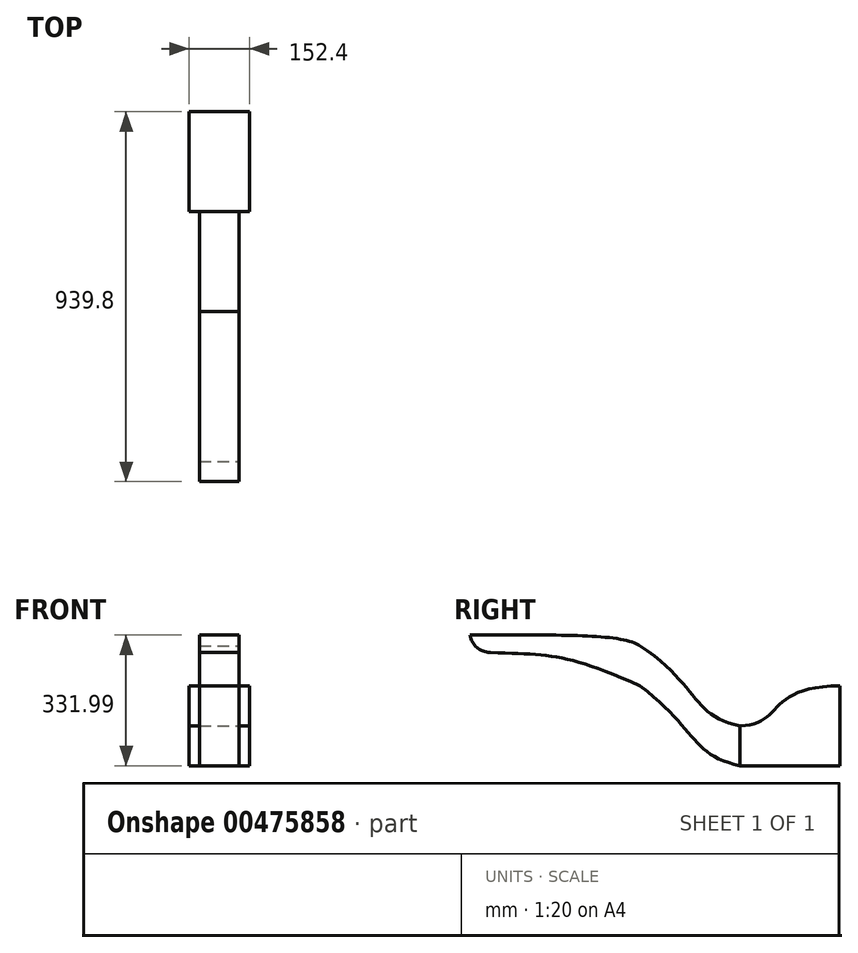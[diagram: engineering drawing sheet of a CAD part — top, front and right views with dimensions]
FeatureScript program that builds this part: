
annotation { "Feature Type Name" : "Feature", "Feature Type Description" : "" }
export const myFeature = defineFeature(function(context is Context, id is Id, definition is map)
    precondition{}
    {
        {
            var Q0;
            Q0=qCreatedBy(makeId("Top.planeOp"),FACE);
            var sketch = newSketch(context, id + "F0", { "sketchPlane" : qUnion([Q0])});
            skLineSegment(sketch, "E0.bottom", {"start": v(63.5, -381) * mm, "end": v(-63.5, -381) * mm});
            skLineSegment(sketch, "E0.top", {"start": v(63.5, 381) * mm, "end": v(-63.5, 381) * mm});
            skLineSegment(sketch, "E0.left", {"start": v(63.5, -381) * mm, "end": v(63.5, 381) * mm});
            skLineSegment(sketch, "E0.right", {"start": v(-63.5, -381) * mm, "end": v(-63.5, 381) * mm});
            skPoint(sketch, "E0.middle", {"position": v(0, 0) * mm});
            skSolve(sketch);
        }
        {
            var Q0;
            Q0=makeQuery(id+"F0.imprint","IMPRINT",FACE,{"disambiguationData":[TD([[makeQuery(id+"F0.imprint","IMPRINT",EDGE,{"derivedFrom":sQuery(id+"F0.wireOp",EDGE,"E0.bottom")}),-1.0]])]});
            extrude(context, id + "F1", {"entities" : qUnion([Q0]), "depth" : 203.2 * mm});
        }
        {
            var Q0;
            Q0=makeQuery(id+"F1.opExtrude","SWEPT_FACE",FACE,{"disambiguationData":[OSD([sQuery(id+"F0.wireOp",EDGE,"E0.left")])]});
            var sketch = newSketch(context, id + "F2", { "sketchPlane" : qUnion([Q0])});
            skLineSegment(sketch, "E1", {"start": v(381, 0) * mm, "end": v(254, 0) * mm});
            skLineSegment(sketch, "E2", {"start": v(127, 0) * mm, "end": v(381, 0) * mm});
            skLineSegment(sketch, "E3", {"start": v(254, 0) * mm, "end": v(127, 0) * mm});
            skLineSegment(sketch, "E4", {"start": v(127, 0) * mm, "end": v(127, 0) * mm});
            skFitSpline(sketch, "E5", {"points": [v(-127, 203.2) * mm, v(127, 0) * mm], "startDerivative": vector(433.66, -329.5) * mm, "endDerivative": vector(381, -83.25) * mm});
            skPoint(sketch, "E6.middle", {"position": v(-271.55, 313.03) * mm});
            skPoint(sketch, "E7", {"position": v(-507.66, 288.1) * mm});
            skFitSpline(sketch, "E8", {"points": [v(-507.66, 288.1) * mm, v(-127, 203.2) * mm], "startDerivative": vector(459.22, -20.75) * mm, "endDerivative": vector(582.11, -257.2) * mm});
            skFitSpline(sketch, "E9", {"points": [v(127, 101.6) * mm, v(381, 203.2) * mm], "startDerivative": vector(325.8, 0) * mm, "endDerivative": vector(566.62, 0) * mm});
            skPoint(sketch, "E10", {"position": v(254, 101.6) * mm});
            skFitSpline(sketch, "E11", {"points": [v(-127, 304.8) * mm, v(127, 101.6) * mm], "startDerivative": vector(457.45, -304.8) * mm, "endDerivative": vector(381, -78.88) * mm});
            skFitSpline(sketch, "E12", {"points": [v(-127, 304.8) * mm, v(-354.58, 331.99) * mm], "startDerivative": vector(-89.06, 62.37) * mm, "endDerivative": vector(-329.75, 0) * mm});
            skLineSegment(sketch, "E13", {"start": v(-354.58, 331.99) * mm, "end": v(-507.66, 331.99) * mm});
            skLineSegment(sketch, "E14", {"start": v(-507.66, 331.99) * mm, "end": v(-551.54, 331.99) * mm});
            skPoint(sketch, "E15", {"position": v(-431.12, 331.99) * mm});
            skLineSegment(sketch, "E16", {"start": v(127, 101.6) * mm, "end": v(127, 0) * mm});
            skLineSegment(sketch, "E17", {"start": v(381, 203.2) * mm, "end": v(381, 331.99) * mm});
            skLineSegment(sketch, "E18", {"start": v(-507.66, 331.99) * mm, "end": v(-558.8, 331.99) * mm});
            skPoint(sketch, "E18.endSnap0", {"position": v(-529.6, 331.99) * mm});
            skLineSegment(sketch, "E19", {"start": v(-558.8, 331.99) * mm, "end": v(-558.8, 288.1) * mm});
            skLineSegment(sketch, "E20", {"start": v(-558.8, 288.1) * mm, "end": v(-507.66, 288.1) * mm});
            skSolve(sketch);
        }
        {
            var Q0;
            Q0=makeQuery(id+"F1.opExtrude","CAP_FACE",FACE,{"disambiguationData":[OSD([sQuery(id+"F0.wireOp",EDGE,"E0.bottom"),sQuery(id+"F0.wireOp",EDGE,"E0.top"),sQuery(id+"F0.wireOp",EDGE,"E0.left"),sQuery(id+"F0.wireOp",EDGE,"E0.right")])],"isStart":false});
            extrude(context, id + "F3", {"entities" : qUnion([Q0]), "operationType" : NewBodyOperationType.ADD, "depth" : 304.8 * mm});
        }
        {
            var Q0;
            {var subQ0=sQuery(id+"F0.wireOp",EDGE,"E0.bottom");Q0=makeQuery(id+"F3.boolean.opBoolean","MERGE",FACE,{"derivedFrom":[makeQuery(id+"F1.opExtrude","SWEPT_FACE",FACE,{"disambiguationData":[OSD([subQ0])]}),makeQuery(id+"F3.opExtrude","SWEPT_FACE",FACE,{"disambiguationData":[OSD([subQ0])]})]});}
            extrude(context, id + "F4", {"entities" : qUnion([Q0]), "operationType" : NewBodyOperationType.ADD, "depth" : 304.8 * mm});
        }
        {
            var Q0;
            {var subQ0=sQuery(id+"F0.wireOp",EDGE,"E0.left");Q0=makeQuery(id+"F4.boolean.opBoolean","MERGE",FACE,{"derivedFrom":[makeQuery(id+"F3.boolean.opBoolean","MERGE",FACE,{"derivedFrom":[makeQuery(id+"F1.opExtrude","SWEPT_FACE",FACE,{"disambiguationData":[OSD([subQ0])]}),makeQuery(id+"F3.opExtrude","SWEPT_FACE",FACE,{"disambiguationData":[OSD([subQ0])]})]}),makeQuery(id+"F4.opExtrude","SWEPT_FACE",FACE,{"disambiguationData":[OSD([sQuery(id+"F0.wireOp",EDGE,"E0.bottom"),subQ0])]})]});}
            extrude(context, id + "F5", {"entities" : qUnion([Q0]), "operationType" : NewBodyOperationType.REMOVE, "oppositeDirection" : true, "depth" : 127 * mm});
        }
        {
            var Q0;
            Q0=makeQuery(id+"F2.imprint","IMPRINT",FACE,{"disambiguationData":[TD([[makeQuery(id+"F2.imprint","IMPRINT",EDGE,{"derivedFrom":sQuery(id+"F2.wireOp",EDGE,"E2")}),1.0]])]});
            extrude(context, id + "F6", {"entities" : qUnion([Q0]), "depth" : 25.4 * mm, "hasSecondDirection" : true, "secondDirectionOppositeDirection" : true, "secondDirectionDepth" : 127 * mm});
        }
        {
            var Q0;
            {var subQ1=sQuery(id+"F2.wireOp",EDGE,"E8");Q0=makeQuery(id+"F2.imprint","IMPRINT",FACE,{"disambiguationData":[TD([[makeQuery(id+"F2.imprint","IMPRINT",EDGE,{"derivedFrom":subQ1}),1.0]])]});}
            var Q1;
            {var subQ0=sQuery(id+"F2.wireOp",EDGE,"E5");Q1=makeQuery(id+"F2.imprint","IMPRINT",FACE,{"disambiguationData":[TD([[makeQuery(id+"F2.imprint","IMPRINT",EDGE,{"derivedFrom":subQ0}),1.0]])]});}
            extrude(context, id + "F7", {"entities" : qUnion([Q0, Q1]), "operationType" : NewBodyOperationType.ADD, "oppositeDirection" : true, "depth" : 101.6 * mm});
        }
        {
            var Q0;
            Q0=makeQuery(id+"F7.opExtrude","SWEPT_EDGE",EDGE,{"disambiguationData":[OSD([sQuery(id+"F2.wireOp",EDGE,"E19"),sQuery(id+"F2.wireOp",EDGE,"E20")])]});
            fillet(context, id + "F8", {"entities" : qUnion([Q0]), "radius" : 50.8 * mm, "tangentPropagation" : true, "allowEdgeOverflow" : false});
        }
    });
